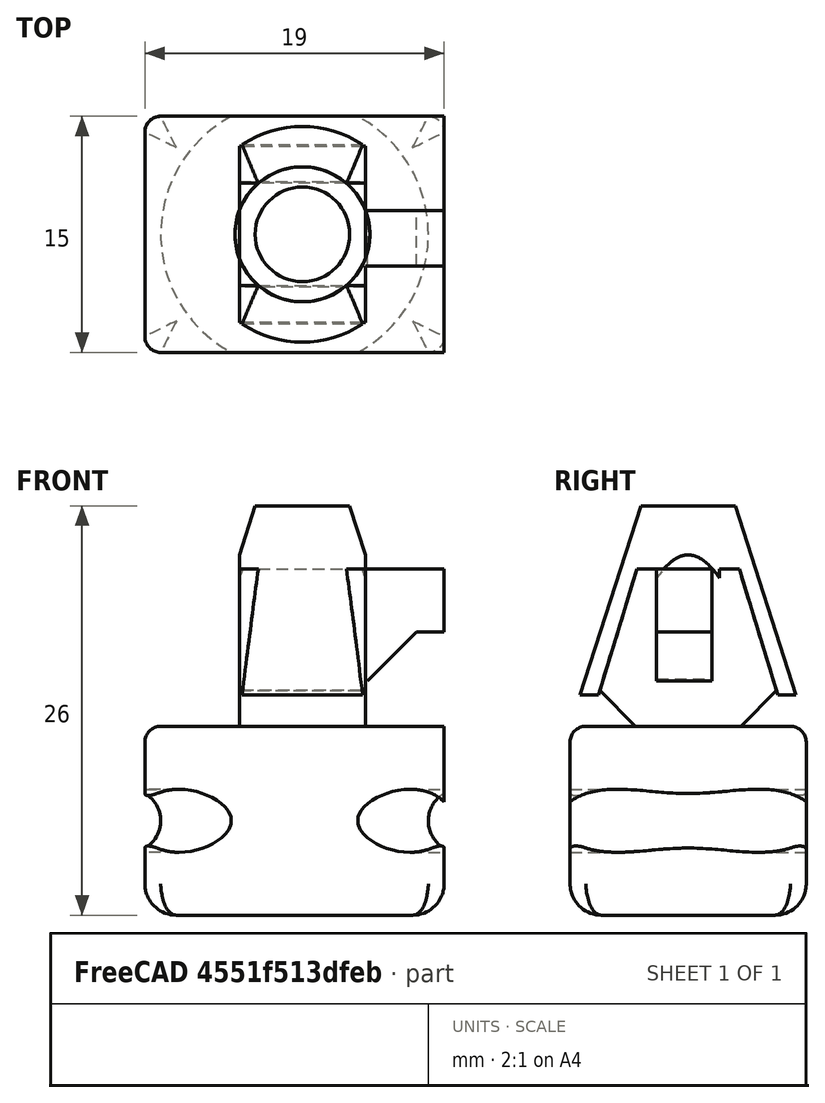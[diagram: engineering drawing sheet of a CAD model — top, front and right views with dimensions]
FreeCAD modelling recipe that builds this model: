
FCSTD DOCUMENT  (FreeCAD 0.16R6707 (Git))
Label: Soporte_maletero_corsa_v2
License: CC-BY 3.0
LicenseURL: http://creativecommons.org/licenses/by/3.0/
objects: Part::Box×18, Part::Cut×14, Part::Fillet×6, Part::MultiFuse×3, Part::Cone×1, Part::Torus×1
note: 43 computed .brp shape members not serialized (recipe doc carries the construction recipe); baked Part::Feature solids carry a one-line shape summary decoded from their .brp

FEATURE [Part::Cone] Cone
  Angle = 360
  Height = 14
  Radius1 = 7.5
  Radius2 = 3
FEATURE [Part::Box] Box
  Height = 10
  Length = 20
  Placement = pos=(0,12,0) rot=(0,0,1;0rad)
  Width = 5
FEATURE [Part::Box] Box001
  Height = 18
  Length = 20
  Placement = pos=(0,17.17,-2.83) rot=(1,0,0;0.296705rad)
  Width = 8
FEATURE [Part::Cut] Cut  label="Cuña"
  Base = -> Box
  Placement = pos=(-10,-10,0) rot=(0,0,1;0rad)
  Tool = -> Box001
FEATURE [Part::Box] Box002
  Height = 18
  Length = 8
  Placement = pos=(-4,17.17,-2.83) rot=(1,0,0;0.296706rad)
  Width = 8
FEATURE [Part::Box] Box003
  Height = 10
  Length = 8
  Placement = pos=(-4,12,0) rot=(0,0,1;0rad)
  Width = 5
FEATURE [Part::Cut] Cut001  label="Cuña001"
  Base = -> Box003
  Placement = pos=(0,10,0) rot=(0,0,1;3.14159rad)
  Tool = -> Box002
FEATURE [Part::Cut] Cut002
  Base = -> Cone
  Tool = -> Cut
FEATURE [Part::Cut] Cut003
  Base = -> Cut002
  Tool = -> Cut001
FEATURE [Part::Box] Box004
  Height = 4
  Length = 12
  Placement = pos=(-3,-2,6) rot=(0,0,1;0rad)
  Width = 3.5
FEATURE [Part::Box] Box005
  Height = 15
  Length = 10
  Placement = pos=(4,-4,0) rot=(0,0,1;0rad)
  Width = 10
FEATURE [Part::Box] Box006
  Height = 15
  Length = 10
  Placement = pos=(-4,-4,0) rot=(0,0,1;1.5708rad)
  Width = 10
FEATURE [Part::Cut] Cut004
  Base = -> Cut003
  Tool = -> Box005
FEATURE [Part::Cut] Cut005
  Base = -> Cut004
  Tool = -> Box006
FEATURE [Part::Box] Box007
  Height = 12
  Length = 19
  Placement = pos=(-10,-7.5,-12) rot=(0,0,1;0rad)
  Width = 15
FEATURE [Part::Box] Box008
  Height = 5
  Length = 10
  Placement = pos=(-5,5,-3) rot=(0,0,1;0rad)
  Width = 10
FEATURE [Part::Box] Box009
  Height = 5
  Length = 10
  Placement = pos=(5,-4,-3) rot=(0,0,1;3.14159rad)
  Width = 10
FEATURE [Part::Cut] Cut006
  Base = -> Cut005
  Tool = -> Box009
FEATURE [Part::Cut] Cut007
  Base = -> Cut006
  Tool = -> Box008
FEATURE [Part::Torus] Torus
  Angle1 = -180
  Angle2 = 180
  Angle3 = 360
  Placement = pos=(-0.5,0,-6) rot=(0,0,1;0rad)
  Radius1 = 10.5
  Radius2 = 2
FEATURE [Part::Cut] Cut008
  Base = -> Box007
  Tool = -> Torus
FEATURE [Part::MultiFuse] Fusion
  Shapes = -> [Box004,Cut007,Cut008]
FEATURE [Part::Fillet] Fillet
  Base = -> Fusion
  Edges = 4 edges r=2: [Edge56,Edge62,Edge72,Edge74]
FEATURE [Part::Fillet] Fillet001
  Base = -> Fillet
  Edges = 1 edges r=1: [Edge27]
FEATURE [Part::Fillet] Fillet002
  Base = -> Fillet001
  Edges = 1 edges r=1: [Edge19]
FEATURE [Part::Fillet] Fillet003
  Base = -> Fillet002
  Edges = 1 edges r=1: [Edge8]
FEATURE [Part::Fillet] Fillet004
  Base = -> Fillet003
  Edges = 1 edges r=1: [Edge54]
FEATURE [Part::Fillet] Fillet005
  Base = -> Fillet004
  Edges = 3 edges r=1: [Edge6,Edge25,Edge36]
FEATURE [Part::Box] Box010
  Height = 18
  Length = 8
  Placement = pos=(-4,17.17,-2.83) rot=(1,0,0;0.296706rad)
  Width = 8
FEATURE [Part::Box] Box011
  Height = 10
  Length = 8
  Placement = pos=(-4,12,0) rot=(0,0,1;0rad)
  Width = 5
FEATURE [Part::Cut] Cut009  label="Cuña002"
  Base = -> Box011
  Placement = pos=(0,10,0) rot=(0,0,1;3.14159rad)
  Tool = -> Box010
FEATURE [Part::Box] Box012  label="Cubo"
  Height = 4
  Length = 8
  Placement = pos=(-4,-10,1) rot=(-1,0,0;0.785398rad)
  Width = 7
FEATURE [Part::Cut] Cut010
  Base = -> Cut009
  Tool = -> Box012
FEATURE [Part::Box] Box013
  Height = 18
  Length = 8
  Placement = pos=(-4,17.17,-2.83) rot=(1,0,0;0.296706rad)
  Width = 8
FEATURE [Part::Box] Box014
  Height = 10
  Length = 8
  Placement = pos=(-4,12,0) rot=(0,0,1;0rad)
  Width = 5
FEATURE [Part::Cut] Cut011  label="Cuña003"
  Base = -> Box014
  Placement = pos=(0,10,0) rot=(0,0,1;3.14159rad)
  Tool = -> Box013
FEATURE [Part::Box] Box015  label="Cubo001"
  Height = 4
  Length = 8
  Placement = pos=(-4,-10,1) rot=(-1,0,0;0.785398rad)
  Width = 7
FEATURE [Part::Cut] Cut012
  Base = -> Cut011
  Placement = pos=(0,0,0) rot=(0,0,1;3.14159rad)
  Tool = -> Box015
FEATURE [Part::Box] Box016  label="Cubo002"
  Height = 5
  Length = 5
  Placement = pos=(4,-5,0) rot=(0,0,1;0rad)
  Width = 10
FEATURE [Part::Cut] Cut013
  Base = -> Fillet005
  Tool = -> Box016
FEATURE [Part::Box] Box017  label="Cubo003"
  Height = 5
  Length = 3
  Placement = pos=(2,-2,5) rot=(0,1,0;0.785398rad)
  Width = 3.5
FEATURE [Part::MultiFuse] Fusion001
  Shapes = -> [Cut010,Cut012,Box017,Cut013]
FEATURE [Part::MultiFuse] Fusion002
  Shapes = -> [Box004,Fusion001]
